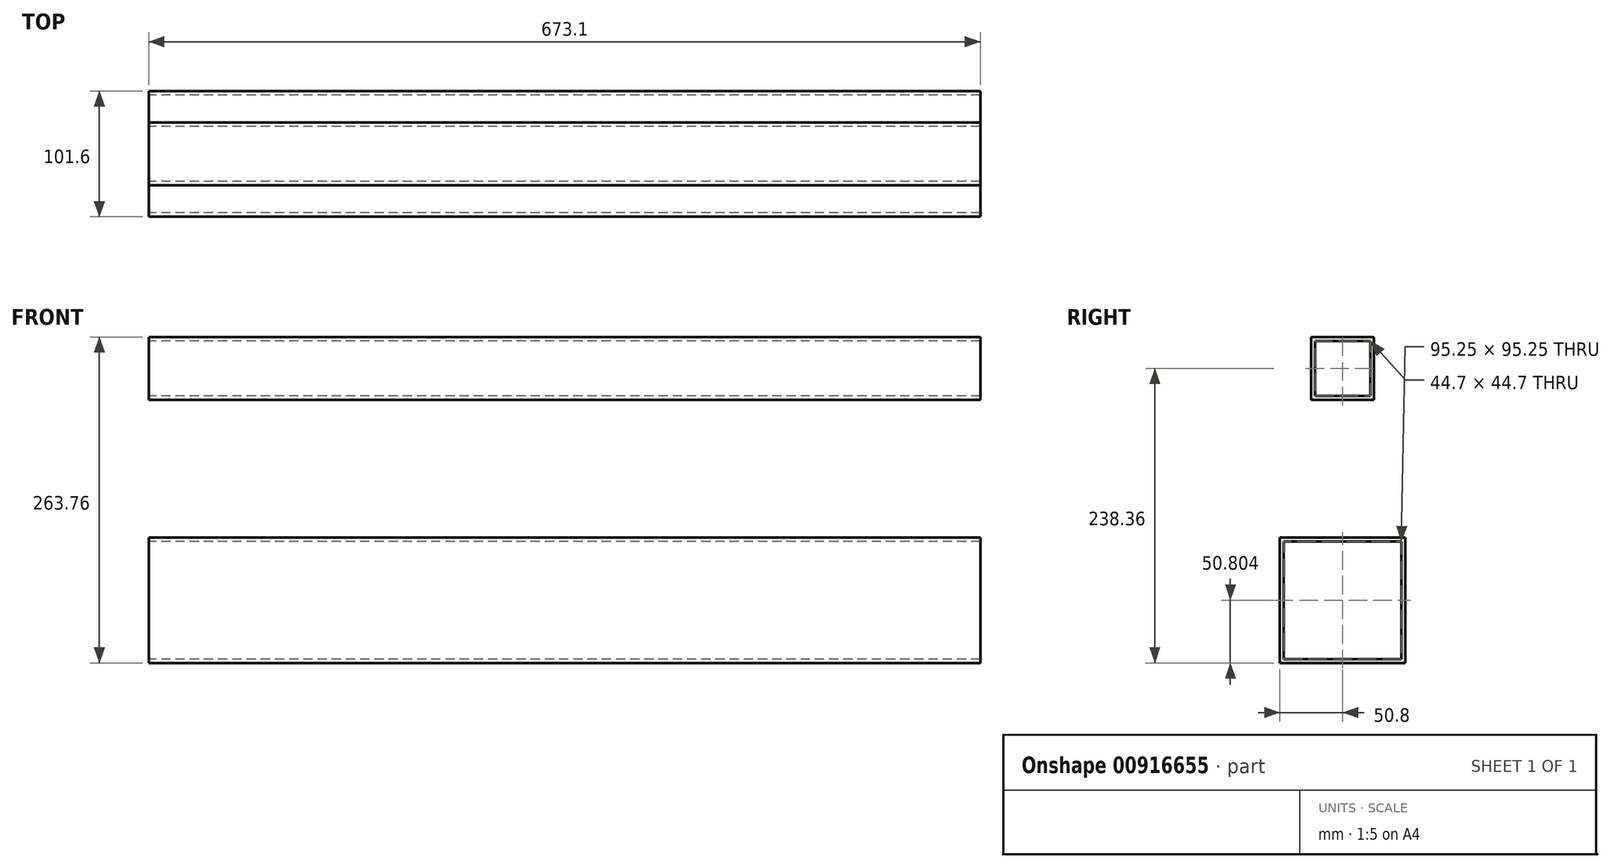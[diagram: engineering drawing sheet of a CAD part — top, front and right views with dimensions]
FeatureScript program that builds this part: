
annotation { "Feature Type Name" : "Feature", "Feature Type Description" : "" }
export const myFeature = defineFeature(function(context is Context, id is Id, definition is map)
    precondition{}
    {
        {
            var Q0;
            Q0=qCreatedBy(makeId("Right.planeOp"),FACE);
            var sketch = newSketch(context, id + "F0", { "sketchPlane" : qUnion([Q0])});
            skLineSegment(sketch, "E0.bottom", {"start": v(25.4, 25.4) * mm, "end": v(-25.4, 25.4) * mm});
            skLineSegment(sketch, "E0.top", {"start": v(25.4, -25.4) * mm, "end": v(-25.4, -25.4) * mm});
            skLineSegment(sketch, "E0.left", {"start": v(25.4, 25.4) * mm, "end": v(25.4, -25.4) * mm});
            skLineSegment(sketch, "E0.right", {"start": v(-25.4, 25.4) * mm, "end": v(-25.4, -25.4) * mm});
            skPoint(sketch, "E0.middle", {"position": v(0, 0) * mm});
            skLineSegment(sketch, "E1.bottom", {"start": v(-22.35, 22.35) * mm, "end": v(22.35, 22.35) * mm});
            skLineSegment(sketch, "E1.top", {"start": v(-22.35, -22.35) * mm, "end": v(22.35, -22.35) * mm});
            skLineSegment(sketch, "E1.left", {"start": v(-22.35, 22.35) * mm, "end": v(-22.35, -22.35) * mm});
            skLineSegment(sketch, "E1.right", {"start": v(22.35, 22.35) * mm, "end": v(22.35, -22.35) * mm});
            skSolve(sketch);
        }
        {
            var Q0;
            Q0 = qSketchRegion(id + "F0", true);
            extrude(context, id + "F1", {"entities" : qUnion([Q0]), "depth" : 673.1 * mm, "offsetDistance" : 25.4 * mm});
        }
        {
            var Q0;
            Q0=qCreatedBy(makeId("Right.planeOp"),FACE);
            var sketch = newSketch(context, id + "F2", { "sketchPlane" : qUnion([Q0])});
            skLineSegment(sketch, "E2.bottom", {"start": v(50.8, -136.76) * mm, "end": v(-50.8, -136.76) * mm});
            skLineSegment(sketch, "E2.top", {"start": v(50.8, -238.36) * mm, "end": v(-50.8, -238.36) * mm});
            skLineSegment(sketch, "E2.left", {"start": v(50.8, -136.76) * mm, "end": v(50.8, -238.36) * mm});
            skLineSegment(sketch, "E2.right", {"start": v(-50.8, -136.76) * mm, "end": v(-50.8, -238.36) * mm});
            skPoint(sketch, "E2.middle", {"position": v(0, -187.56) * mm});
            skLineSegment(sketch, "E3.bottom", {"start": v(-47.63, -139.93) * mm, "end": v(47.63, -139.93) * mm});
            skLineSegment(sketch, "E3.top", {"start": v(-47.63, -235.18) * mm, "end": v(47.63, -235.18) * mm});
            skLineSegment(sketch, "E3.left", {"start": v(-47.63, -139.93) * mm, "end": v(-47.63, -235.18) * mm});
            skLineSegment(sketch, "E3.right", {"start": v(47.63, -139.93) * mm, "end": v(47.63, -235.18) * mm});
            skSolve(sketch);
        }
        {
            var Q0;
            Q0 = qSketchRegion(id + "F2", true);
            extrude(context, id + "F3", {"entities" : qUnion([Q0]), "depth" : 673.1 * mm, "offsetDistance" : 25.4 * mm});
        }
    });
